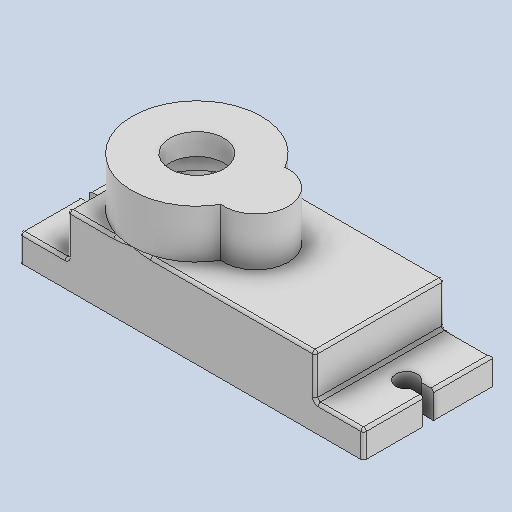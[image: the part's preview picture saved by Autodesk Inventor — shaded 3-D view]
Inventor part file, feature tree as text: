
AUTODESK INVENTOR PART (.ipt)
format: ipt  version: 2025.2 (Build 292293000, 293)  size: 871,424 bytes
history: native  units: mm
features: other x1, thread x1
ambient origin geometry x8: Origin, YZ Plane, XZ Plane, XY Plane, X Axis, Y Axis, Z Axis, Center Point
bodies: Body1 (feature_tree)
feature tree (2):
  other  "Bryła1"
  thread  "Thread4"  [1 undecoded]
note: 1 required parameter value undecoded (feature->parameter linkage not recoverable at this tier; creation-order binding heuristic only, values carry confidence <= 0.55)
